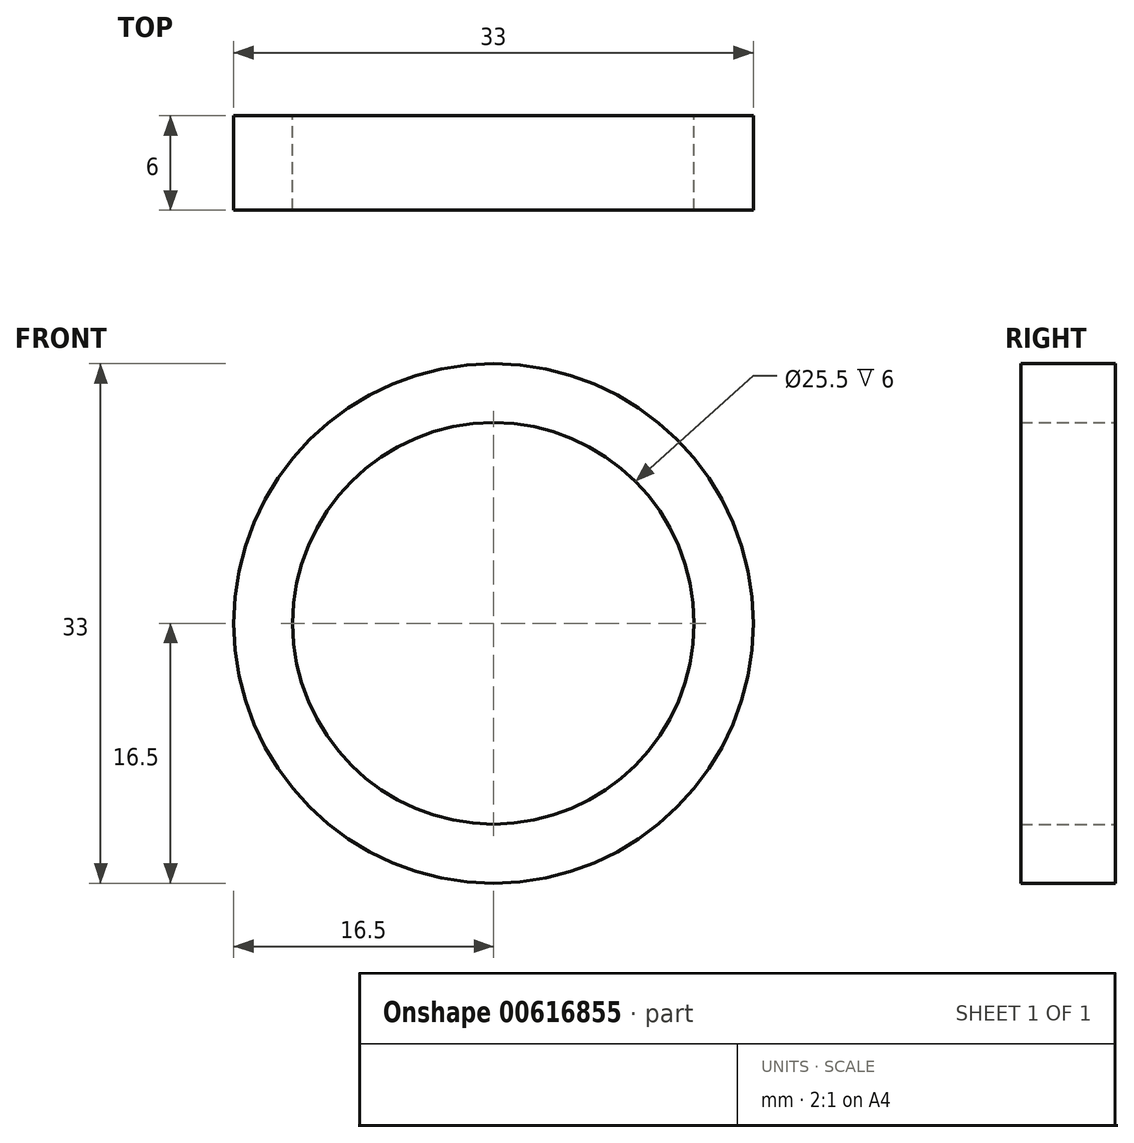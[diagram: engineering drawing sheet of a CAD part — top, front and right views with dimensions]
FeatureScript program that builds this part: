
annotation { "Feature Type Name" : "Feature", "Feature Type Description" : "" }
export const myFeature = defineFeature(function(context is Context, id is Id, definition is map)
    precondition{}
    {
        {
            var Q0;
            Q0=qCreatedBy(makeId("Front.planeOp"),FACE);
            var sketch = newSketch(context, id + "F0", { "sketchPlane" : qUnion([Q0])});
            skCircle(sketch, "E0", {"center": v(0, 0) * mm, "radius": 12.75 * mm});
            skCircle(sketch, "E1", {"center": v(0, 0) * mm, "radius": 16.5 * mm});
            skSolve(sketch);
        }
        {
            var Q0;
            Q0 = qSketchRegion(id + "F0", true);
            extrude(context, id + "F1", {"entities" : qUnion([Q0]), "depth" : 6 * mm, "offsetDistance" : 25 * mm});
        }
    });
